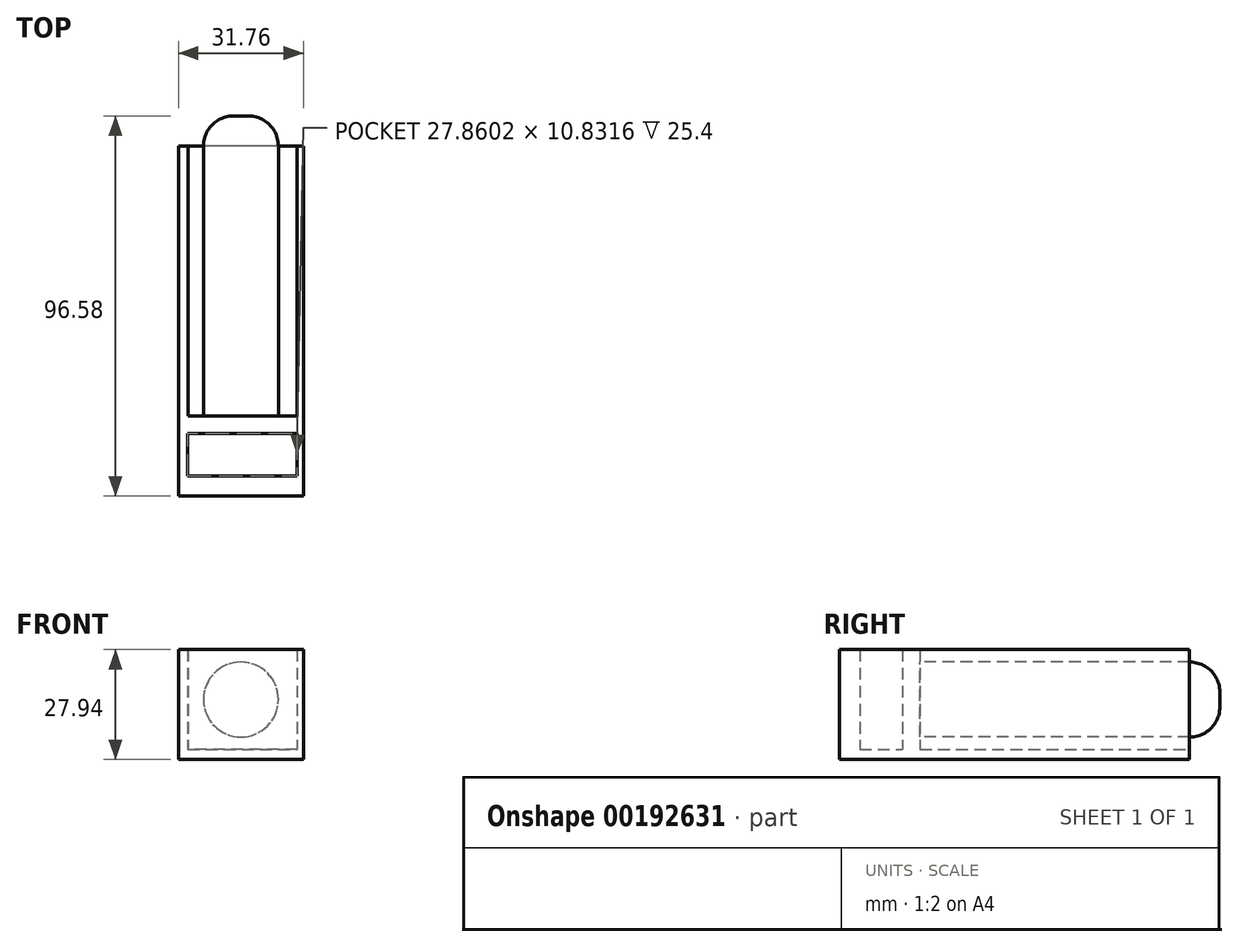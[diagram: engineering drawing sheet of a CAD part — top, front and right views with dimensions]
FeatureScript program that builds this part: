
annotation { "Feature Type Name" : "Feature", "Feature Type Description" : "" }
export const myFeature = defineFeature(function(context is Context, id is Id, definition is map)
    precondition{}
    {
        {
            var Q0;
            Q0=qCreatedBy(makeId("Top.planeOp"),FACE);
            var sketch = newSketch(context, id + "F0", { "sketchPlane" : qUnion([Q0])});
            skLineSegment(sketch, "E0.bottom", {"start": v(15.88, 44.45) * mm, "end": v(-15.87, 44.45) * mm});
            skLineSegment(sketch, "E0.top", {"start": v(15.87, -44.45) * mm, "end": v(-15.88, -44.45) * mm});
            skLineSegment(sketch, "E0.left", {"start": v(15.88, 44.45) * mm, "end": v(15.87, -44.45) * mm});
            skLineSegment(sketch, "E0.right", {"start": v(-15.87, 44.45) * mm, "end": v(-15.88, -44.45) * mm});
            skPoint(sketch, "E0.middle", {"position": v(0, 0) * mm});
            skSolve(sketch);
        }
        {
            var Q0;
            Q0 = qSketchRegion(id + "F0", true);
            extrude(context, id + "F1", {"entities" : qUnion([Q0]), "depth" : 2.54 * mm});
        }
        {
            var Q0;
            Q0=makeQuery(id+"F1.opExtrude","CAP_FACE",FACE,{"disambiguationData":[OSD([sQuery(id+"F0.wireOp",EDGE,"E0.bottom"),sQuery(id+"F0.wireOp",EDGE,"E0.top"),sQuery(id+"F0.wireOp",EDGE,"E0.left"),sQuery(id+"F0.wireOp",EDGE,"E0.right")])],"isStart":false});
            var sketch = newSketch(context, id + "F2", { "sketchPlane" : qUnion([Q0])});
            skLineSegment(sketch, "E1.top", {"start": v(16.02, 44.45) * mm, "end": v(-15.64, 44.45) * mm});
            skLineSegment(sketch, "E2", {"start": v(-15.64, 44.45) * mm, "end": v(-15.87, 44.45) * mm});
            skLineSegment(sketch, "E3", {"start": v(15.88, 44.45) * mm, "end": v(16.02, 44.45) * mm});
            skLineSegment(sketch, "E4.bottom", {"start": v(-13.56, -39.35) * mm, "end": v(14.3, -39.35) * mm});
            skLineSegment(sketch, "E4.top", {"start": v(-13.56, -28.52) * mm, "end": v(14.3, -28.52) * mm});
            skLineSegment(sketch, "E4.left", {"start": v(-13.56, -39.35) * mm, "end": v(-13.56, -28.52) * mm});
            skLineSegment(sketch, "E4.right", {"start": v(14.3, -39.35) * mm, "end": v(14.3, -28.52) * mm});
            skLineSegment(sketch, "E5.bottom", {"start": v(14.3, -24.07) * mm, "end": v(-13.43, -24.07) * mm});
            skLineSegment(sketch, "E5.top", {"start": v(14.3, 44.45) * mm, "end": v(-13.43, 44.45) * mm});
            skLineSegment(sketch, "E5.left", {"start": v(14.3, -24.07) * mm, "end": v(14.3, 44.45) * mm});
            skLineSegment(sketch, "E5.right", {"start": v(-13.43, -24.07) * mm, "end": v(-13.43, 44.45) * mm});
            skSolve(sketch);
        }
        {
            var Q0;
            {var subQ0=sQuery(id+"F2.wireOp",EDGE,"E2");Q0=makeQuery(id+"F2.imprint","IMPRINT",FACE,{"disambiguationData":[TD([[makeQuery(id+"F2.imprint","IMPRINT",EDGE,{"derivedFrom":subQ0}),1.0]])]});}
            extrude(context, id + "F3", {"entities" : qUnion([Q0]), "operationType" : NewBodyOperationType.ADD, "depth" : 25.4 * mm});
        }
        {
            var Q0;
            Q0=makeQuery(id+"F3.opExtrude","SWEPT_FACE",FACE,{"disambiguationData":[OSD([sQuery(id+"F2.wireOp",EDGE,"E5.bottom")])]});
            var sketch = newSketch(context, id + "F4", { "sketchPlane" : qUnion([Q0])});
            skCircle(sketch, "E6", {"center": v(0, 15.24) * mm, "radius": 9.53 * mm});
            skSolve(sketch);
        }
        {
            var Q0;
            Q0=makeQuery(id+"F4.imprint","IMPRINT",FACE,{"disambiguationData":[TD([[makeQuery(id+"F4.imprint","IMPRINT",EDGE,{"derivedFrom":sQuery(id+"F4.wireOp",EDGE,"E6")}),1.0]])]});
            extrude(context, id + "F5", {"entities" : qUnion([Q0]), "operationType" : NewBodyOperationType.ADD, "depth" : 76.2 * mm});
        }
        {
            var Q0;
            Q0=makeQuery(id+"F5.opExtrude","CAP_EDGE",EDGE,{"disambiguationData":[OSD([sQuery(id+"F4.wireOp",EDGE,"E6")])],"isStart":false});
            fillet(context, id + "F6", {"entities" : qUnion([Q0]), "radius" : 7.62 * mm, "tangentPropagation" : true, "allowEdgeOverflow" : false});
        }
    });
